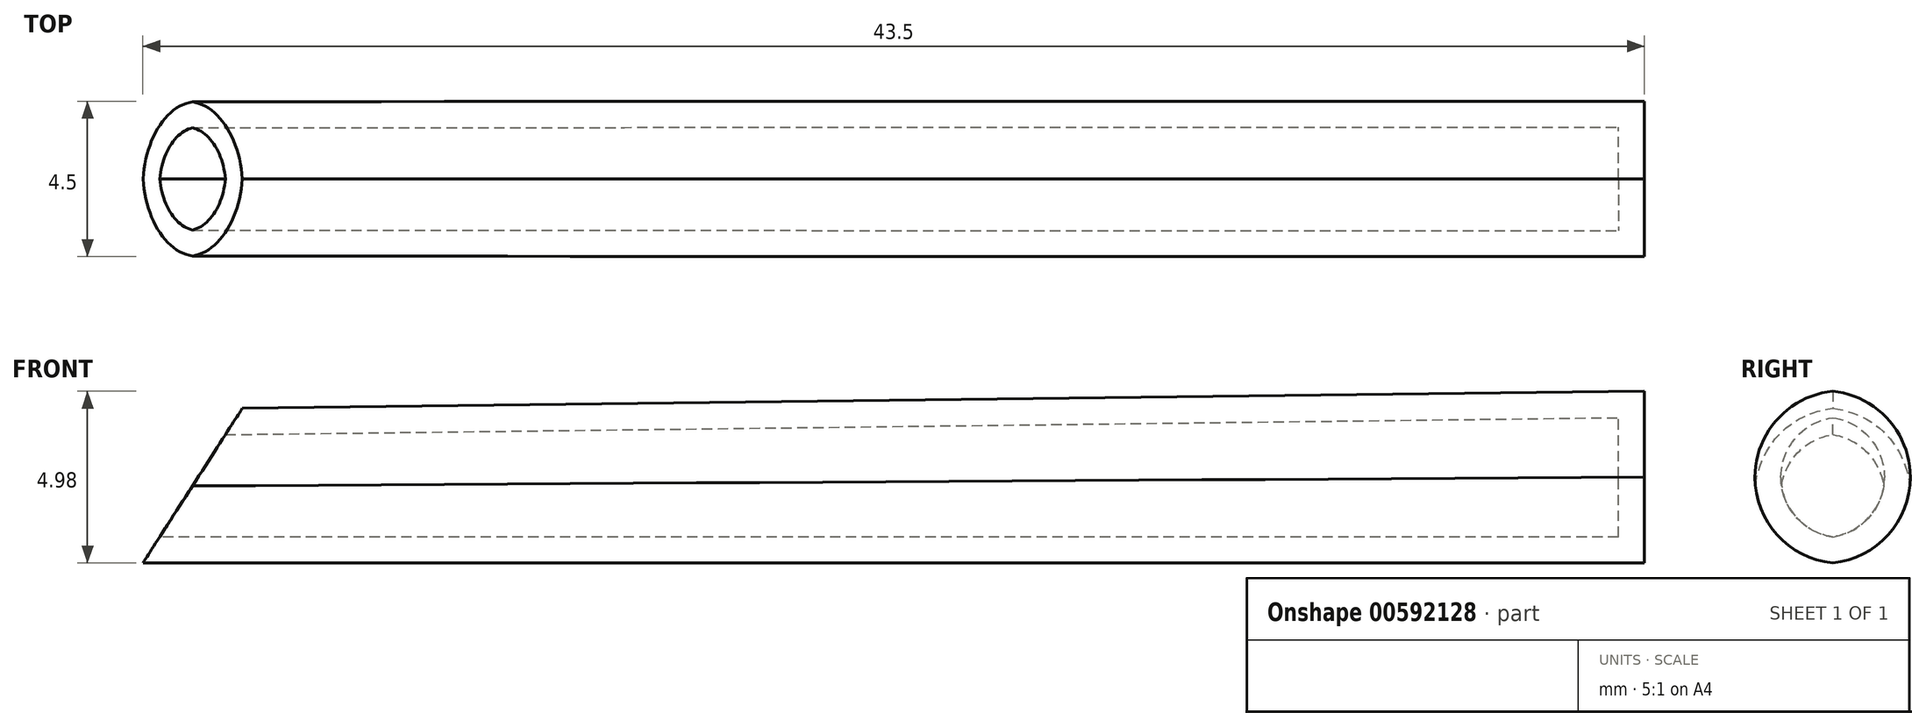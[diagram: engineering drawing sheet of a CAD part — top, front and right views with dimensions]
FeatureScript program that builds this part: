
annotation { "Feature Type Name" : "Feature", "Feature Type Description" : "" }
export const myFeature = defineFeature(function(context is Context, id is Id, definition is map)
    precondition{}
    {
        {
            var Q0;
            Q0=qCreatedBy(makeId("Front.planeOp"),FACE);
            var sketch = newSketch(context, id + "F0", { "sketchPlane" : qUnion([Q0])});
            skLineSegment(sketch, "E0", {"start": v(-41.53, 0) * mm, "end": v(45.47, 0) * mm});
            skLineSegment(sketch, "E1", {"start": v(45.47, 0) * mm, "end": v(45.47, 10) * mm});
            skLineSegment(sketch, "E2", {"start": v(-41.53, 0) * mm, "end": v(-35.74, 9) * mm});
            skLineSegment(sketch, "E3", {"start": v(-35.74, 9) * mm, "end": v(45.47, 10) * mm});
            skSolve(sketch);
        }
        {
            var Q0;
            Q0 = qSketchRegion(id + "F0", true);
            extrude(context, id + "F1", {"entities" : qUnion([Q0]), "depth" : 9 * mm, "offsetDistance" : 25 * mm});
        }
        {
            var Q0;
            Q0=makeQuery(id+"F1.opExtrude","CAP_EDGE",EDGE,{"disambiguationData":[OSD([sQuery(id+"F0.wireOp",EDGE,"E3")])],"isStart":true});
            var Q1;
            Q1=makeQuery(id+"F1.opExtrude","CAP_EDGE",EDGE,{"disambiguationData":[OSD([sQuery(id+"F0.wireOp",EDGE,"E3")])],"isStart":false});
            var Q2;
            Q2=makeQuery(id+"F1.opExtrude","CAP_EDGE",EDGE,{"disambiguationData":[OSD([sQuery(id+"F0.wireOp",EDGE,"E0")])],"isStart":false});
            var Q3;
            Q3=makeQuery(id+"F1.opExtrude","CAP_EDGE",EDGE,{"disambiguationData":[OSD([sQuery(id+"F0.wireOp",EDGE,"E0")])],"isStart":true});
            fillet(context, id + "F2", {"entities" : qUnion([Q0, Q1, Q2, Q3]), "radius" : 5 * mm, "tangentPropagation" : true, "allowEdgeOverflow" : false});
        }
        {
            var Q0;
            Q0=makeQuery(id+"F1.opExtrude","SWEPT_FACE",FACE,{"disambiguationData":[OSD([sQuery(id+"F0.wireOp",EDGE,"E2")])]});
            var Q1;
            Q1=makeQuery(id+"F1.opExtrude","SWEPT_BODY",BODY,{"disambiguationData":[OSD([sQuery(id+"F0.wireOp",EDGE,"E0"),sQuery(id+"F0.wireOp",EDGE,"E1"),sQuery(id+"F0.wireOp",EDGE,"E2"),sQuery(id+"F0.wireOp",EDGE,"E3")])]});
            shell(context, id + "F3", {"entities" : qUnion([Q0]), "parts" : qUnion([Q1]), "thickness" : 1.5 * mm});
        }
        {
            var Q0;
            Q0=makeQuery(id+"F1.opExtrude","SWEPT_BODY",BODY,{"disambiguationData":[OSD([sQuery(id+"F0.wireOp",EDGE,"E0"),sQuery(id+"F0.wireOp",EDGE,"E1"),sQuery(id+"F0.wireOp",EDGE,"E2"),sQuery(id+"F0.wireOp",EDGE,"E3")])]});
            var Q1;
            Q1=qCreatedBy(makeId("Origin.pointOp"),VERTEX);
            transform(context, id + "F4", {"entities" : qUnion([Q0]), "transformType" : TransformType.SCALE_UNIFORMLY, "scale" : .5, "scalePoint" : qUnion([Q1]), "makeCopy" : false});
        }
    });
